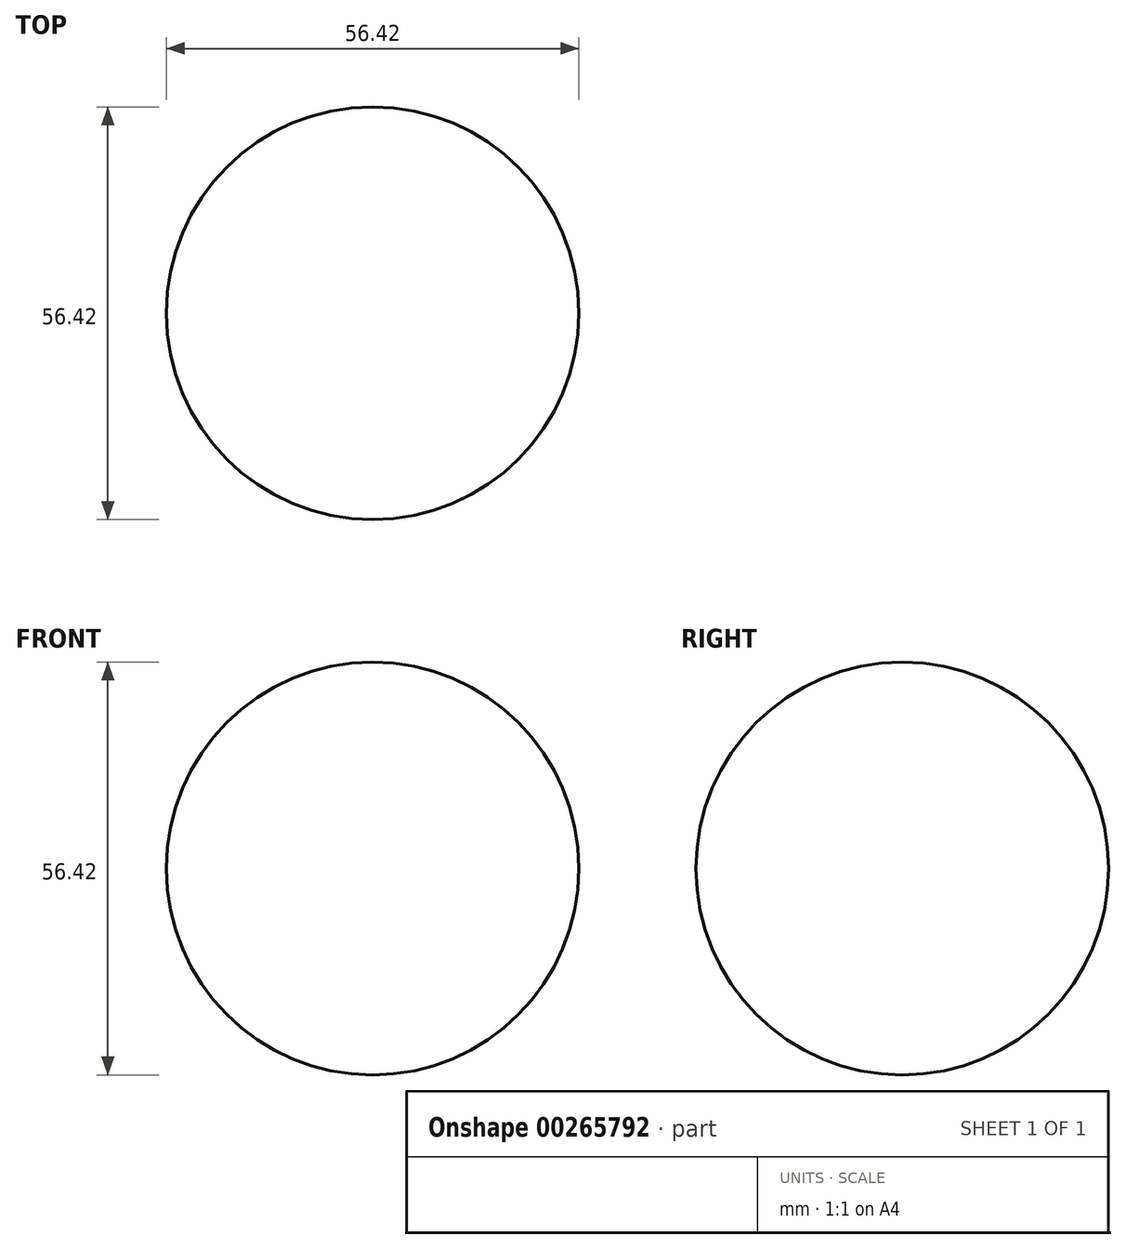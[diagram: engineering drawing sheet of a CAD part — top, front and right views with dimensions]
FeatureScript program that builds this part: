
annotation { "Feature Type Name" : "Feature", "Feature Type Description" : "" }
export const myFeature = defineFeature(function(context is Context, id is Id, definition is map)
    precondition{}
    {
        {
            var Q0;
            Q0=qCreatedBy(makeId("Front.planeOp"),FACE);
            var sketch = newSketch(context, id + "F0", { "sketchPlane" : qUnion([Q0])});
            skArc(sketch, "E0", {"start": v(0, -28.2) * mm, "mid": v(28.2, 0) * mm, "end": v(0, 28.2) * mm});
            skLineSegment(sketch, "E1", {"start": v(0, 28.2) * mm, "end": v(0, -28.2) * mm});
            skSolve(sketch);
        }
        {
            var Q0;
            Q0 = qSketchRegion(id + "F0", true);
            var Q1;
            Q1=sQuery(id+"F0.wireOp",EDGE,"E1");
            revolve(context, id + "F1", {"entities" : qUnion([Q0]), "axis" : qUnion([Q1]), "revolveType" : RevolveType.FULL});
        }
    });
